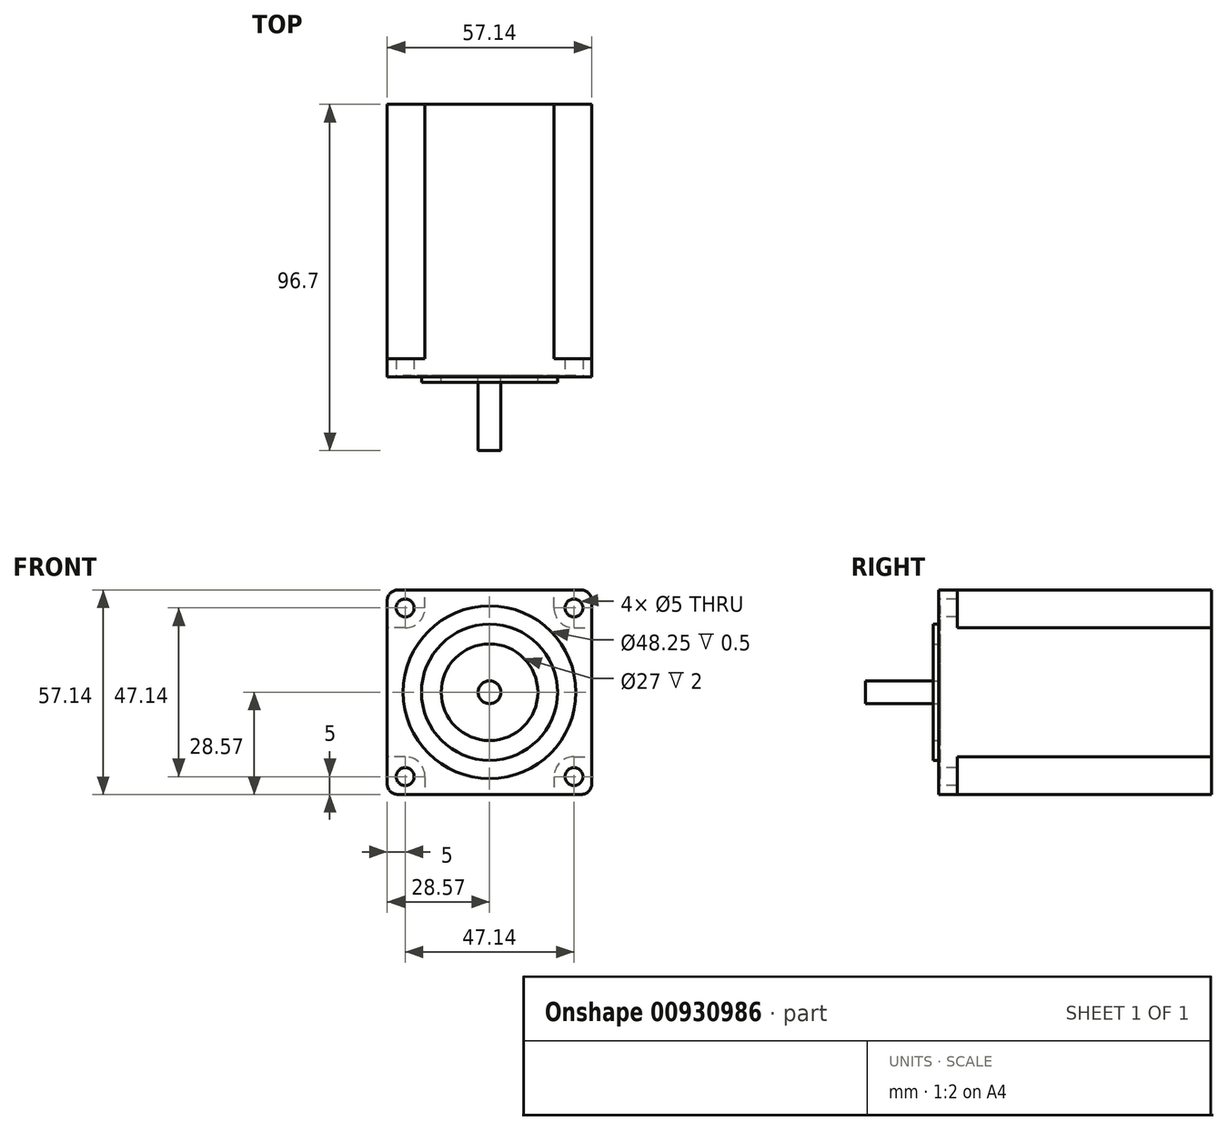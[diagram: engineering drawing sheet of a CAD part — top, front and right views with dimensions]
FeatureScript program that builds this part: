
annotation { "Feature Type Name" : "Feature", "Feature Type Description" : "" }
export const myFeature = defineFeature(function(context is Context, id is Id, definition is map)
    precondition{}
    {
        {
            var Q0;
            Q0=qCreatedBy(makeId("Front.planeOp"),FACE);
            var sketch = newSketch(context, id + "F0", { "sketchPlane" : qUnion([Q0])});
            skLineSegment(sketch, "E0.bottom", {"start": v(28.57, 28.58) * mm, "end": v(-28.58, 28.58) * mm});
            skLineSegment(sketch, "E0.top", {"start": v(28.58, -28.58) * mm, "end": v(-28.57, -28.58) * mm});
            skLineSegment(sketch, "E0.left", {"start": v(28.57, 28.58) * mm, "end": v(28.58, -28.58) * mm});
            skLineSegment(sketch, "E0.right", {"start": v(-28.58, 28.58) * mm, "end": v(-28.57, -28.58) * mm});
            skPoint(sketch, "E0.middle", {"position": v(0, 0) * mm});
            skSolve(sketch);
        }
        {
            var Q0;
            Q0=makeQuery(id+"F0.imprint","IMPRINT",FACE,{"disambiguationData":[TD([[makeQuery(id+"F0.imprint","IMPRINT",EDGE,{"derivedFrom":sQuery(id+"F0.wireOp",EDGE,"E0.bottom")}),1.0]])]});
            extrude(context, id + "F1", {"entities" : qUnion([Q0]), "oppositeDirection" : true, "depth" : 76.2 * mm, "offsetDistance" : 25 * mm});
        }
        {
            var Q0;
            Q0=makeQuery(id+"F1.opExtrude","CAP_FACE",FACE,{"disambiguationData":[OSD([sQuery(id+"F0.wireOp",EDGE,"E0.bottom"),sQuery(id+"F0.wireOp",EDGE,"E0.top"),sQuery(id+"F0.wireOp",EDGE,"E0.left"),sQuery(id+"F0.wireOp",EDGE,"E0.right")])],"isStart":true});
            var sketch = newSketch(context, id + "F2", { "sketchPlane" : qUnion([Q0])});
            skLineSegment(sketch, "E1.bottom", {"start": v(-23.57, 23.57) * mm, "end": v(23.57, 23.57) * mm, "construction": true});
            skLineSegment(sketch, "E1.top", {"start": v(-23.57, -23.57) * mm, "end": v(23.57, -23.57) * mm, "construction": true});
            skLineSegment(sketch, "E1.left", {"start": v(-23.57, 23.57) * mm, "end": v(-23.57, -23.57) * mm, "construction": true});
            skLineSegment(sketch, "E1.right", {"start": v(23.57, 23.57) * mm, "end": v(23.57, -23.57) * mm, "construction": true});
            skPoint(sketch, "E1.middle", {"position": v(0, 0) * mm});
            skCircle(sketch, "E2", {"center": v(-23.57, 23.57) * mm, "radius": 2.5 * mm});
            skCircle(sketch, "E3", {"center": v(23.57, 23.57) * mm, "radius": 2.5 * mm});
            skCircle(sketch, "E4", {"center": v(-23.57, -23.57) * mm, "radius": 2.5 * mm});
            skCircle(sketch, "E5", {"center": v(23.57, -23.57) * mm, "radius": 2.5 * mm});
            skSolve(sketch);
        }
        {
            var Q0;
            Q0 = qSketchRegion(id + "F2", true);
            extrude(context, id + "F3", {"entities" : qUnion([Q0]), "operationType" : NewBodyOperationType.REMOVE, "endBound" : BoundingType.THROUGH_ALL, "oppositeDirection" : true, "depth" : 25 * mm, "offsetDistance" : 25 * mm});
        }
        {
            var Q0;
            Q0=makeQuery(id+"F1.opExtrude","CAP_FACE",FACE,{"disambiguationData":[OSD([sQuery(id+"F0.wireOp",EDGE,"E0.bottom"),sQuery(id+"F0.wireOp",EDGE,"E0.top"),sQuery(id+"F0.wireOp",EDGE,"E0.left"),sQuery(id+"F0.wireOp",EDGE,"E0.right")])],"isStart":false});
            var sketch = newSketch(context, id + "F4", { "sketchPlane" : qUnion([Q0])});
            skArc(sketch, "E6", {"start": v(-23.57, 18.02) * mm, "mid": v(-19.65, 19.65) * mm, "end": v(-18.02, 23.57) * mm});
            skLineSegment(sketch, "E7", {"start": v(-18.02, 23.57) * mm, "end": v(-18.02, 28.58) * mm});
            skLineSegment(sketch, "E8", {"start": v(-23.57, 18.02) * mm, "end": v(-28.57, 18.02) * mm});
            skLineSegment(sketch, "E9", {"start": v(0, 28.58) * mm, "end": v(0, -28.58) * mm, "construction": true});
            skLineSegment(sketch, "E10", {"start": v(0, -28.57) * mm, "end": v(28.57, 0) * mm, "construction": true});
            skLineSegment(sketch, "E11", {"start": v(28.57, 0) * mm, "end": v(-28.57, 0) * mm, "construction": true});
            skLineSegment(sketch, "E12.MirrorCS", {"start": v(18.02, 23.57) * mm, "end": v(18.02, 28.57) * mm});
            skArc(sketch, "E13.MirrorCS", {"start": v(23.57, 18.02) * mm, "mid": v(19.65, 19.65) * mm, "end": v(18.02, 23.57) * mm});
            skLineSegment(sketch, "E14.MirrorCS", {"start": v(23.57, 18.02) * mm, "end": v(28.58, 18.02) * mm});
            skLineSegment(sketch, "E15.MirrorCS", {"start": v(18.02, -23.57) * mm, "end": v(18.02, -28.57) * mm});
            skArc(sketch, "E16.MirrorCS", {"start": v(23.57, -18.02) * mm, "mid": v(19.65, -19.65) * mm, "end": v(18.02, -23.57) * mm});
            skArc(sketch, "E17.MirrorCS", {"start": v(-23.57, -18.02) * mm, "mid": v(-19.65, -19.65) * mm, "end": v(-18.02, -23.57) * mm});
            skLineSegment(sketch, "E18.MirrorCS", {"start": v(23.57, -18.02) * mm, "end": v(28.58, -18.02) * mm});
            skLineSegment(sketch, "E19.MirrorCS", {"start": v(-18.02, -23.57) * mm, "end": v(-18.02, -28.58) * mm});
            skLineSegment(sketch, "E20.MirrorCS", {"start": v(-23.57, -18.02) * mm, "end": v(-28.57, -18.02) * mm});
            skLineSegment(sketch, "E21", {"start": v(-28.57, 18.02) * mm, "end": v(-28.57, 28.58) * mm});
            skLineSegment(sketch, "E22", {"start": v(-28.57, 28.58) * mm, "end": v(-18.02, 28.58) * mm});
            skLineSegment(sketch, "E23", {"start": v(18.02, 28.57) * mm, "end": v(28.58, 28.58) * mm});
            skLineSegment(sketch, "E24", {"start": v(28.58, 28.58) * mm, "end": v(28.58, 18.02) * mm});
            skLineSegment(sketch, "E25", {"start": v(18.02, -28.58) * mm, "end": v(28.57, -28.58) * mm});
            skLineSegment(sketch, "E26", {"start": v(28.57, -28.58) * mm, "end": v(28.58, -18.02) * mm});
            skLineSegment(sketch, "E27", {"start": v(-18.02, -28.58) * mm, "end": v(-28.58, -28.58) * mm});
            skLineSegment(sketch, "E28", {"start": v(-28.58, -28.58) * mm, "end": v(-28.57, -18.02) * mm});
            skSolve(sketch);
        }
        {
            var Q0;
            Q0 = qSketchRegion(id + "F4", true);
            extrude(context, id + "F5", {"entities" : qUnion([Q0]), "operationType" : NewBodyOperationType.REMOVE, "oppositeDirection" : true, "depth" : 71 * mm, "offsetDistance" : 25 * mm});
        }
        {
            var Q0;
            Q0=makeQuery(id+"F5.boolean.opBoolean","COPY",EDGE,{"derivedFrom":makeQuery(id+"F5.opExtrude","SWEPT_EDGE",EDGE,{"disambiguationData":[OSD([sQuery(id+"F0.wireOp",EDGE,"E0.bottom"),sQuery(id+"F4.wireOp",EDGE,"E12.MirrorCS"),sQuery(id+"F4.wireOp",EDGE,"E23")])]})});
            var Q1;
            Q1=makeQuery(id+"F5.boolean.opBoolean","COPY",EDGE,{"derivedFrom":makeQuery(id+"F5.opExtrude","SWEPT_EDGE",EDGE,{"disambiguationData":[OSD([sQuery(id+"F0.wireOp",EDGE,"E0.right"),sQuery(id+"F4.wireOp",EDGE,"E14.MirrorCS"),sQuery(id+"F4.wireOp",EDGE,"E24")])]})});
            var Q2;
            Q2=makeQuery(id+"F1.opExtrude","SWEPT_EDGE",EDGE,{"disambiguationData":[OSD([sQuery(id+"F0.wireOp",EDGE,"E0.bottom"),sQuery(id+"F0.wireOp",EDGE,"E0.right")])]});
            var Q3;
            Q3=makeQuery(id+"F1.opExtrude","SWEPT_EDGE",EDGE,{"disambiguationData":[OSD([sQuery(id+"F0.wireOp",EDGE,"E0.bottom"),sQuery(id+"F0.wireOp",EDGE,"E0.left")])]});
            var Q4;
            Q4=makeQuery(id+"F5.boolean.opBoolean","COPY",EDGE,{"derivedFrom":makeQuery(id+"F5.opExtrude","SWEPT_EDGE",EDGE,{"disambiguationData":[OSD([sQuery(id+"F0.wireOp",EDGE,"E0.bottom"),sQuery(id+"F4.wireOp",EDGE,"E7"),sQuery(id+"F4.wireOp",EDGE,"E22")])]})});
            var Q5;
            Q5=makeQuery(id+"F5.boolean.opBoolean","COPY",EDGE,{"derivedFrom":makeQuery(id+"F5.opExtrude","SWEPT_EDGE",EDGE,{"disambiguationData":[OSD([sQuery(id+"F0.wireOp",EDGE,"E0.left"),sQuery(id+"F4.wireOp",EDGE,"E8"),sQuery(id+"F4.wireOp",EDGE,"E21")])]})});
            var Q6;
            Q6=makeQuery(id+"F1.opExtrude","SWEPT_EDGE",EDGE,{"disambiguationData":[OSD([sQuery(id+"F0.wireOp",EDGE,"E0.top"),sQuery(id+"F0.wireOp",EDGE,"E0.right")])]});
            var Q7;
            Q7=makeQuery(id+"F5.boolean.opBoolean","COPY",EDGE,{"derivedFrom":makeQuery(id+"F5.opExtrude","SWEPT_EDGE",EDGE,{"disambiguationData":[OSD([sQuery(id+"F0.wireOp",EDGE,"E0.right"),sQuery(id+"F4.wireOp",EDGE,"E18.MirrorCS"),sQuery(id+"F4.wireOp",EDGE,"E26")])]})});
            var Q8;
            Q8=makeQuery(id+"F5.boolean.opBoolean","COPY",EDGE,{"derivedFrom":makeQuery(id+"F5.opExtrude","SWEPT_EDGE",EDGE,{"disambiguationData":[OSD([sQuery(id+"F0.wireOp",EDGE,"E0.top"),sQuery(id+"F4.wireOp",EDGE,"E15.MirrorCS"),sQuery(id+"F4.wireOp",EDGE,"E25")])]})});
            var Q9;
            Q9=makeQuery(id+"F1.opExtrude","SWEPT_EDGE",EDGE,{"disambiguationData":[OSD([sQuery(id+"F0.wireOp",EDGE,"E0.top"),sQuery(id+"F0.wireOp",EDGE,"E0.left")])]});
            var Q10;
            Q10=makeQuery(id+"F5.boolean.opBoolean","COPY",EDGE,{"derivedFrom":makeQuery(id+"F5.opExtrude","SWEPT_EDGE",EDGE,{"disambiguationData":[OSD([sQuery(id+"F0.wireOp",EDGE,"E0.left"),sQuery(id+"F4.wireOp",EDGE,"E20.MirrorCS"),sQuery(id+"F4.wireOp",EDGE,"E28")])]})});
            var Q11;
            Q11=makeQuery(id+"F5.boolean.opBoolean","COPY",EDGE,{"derivedFrom":makeQuery(id+"F5.opExtrude","SWEPT_EDGE",EDGE,{"disambiguationData":[OSD([sQuery(id+"F0.wireOp",EDGE,"E0.top"),sQuery(id+"F4.wireOp",EDGE,"E19.MirrorCS"),sQuery(id+"F4.wireOp",EDGE,"E27")])]})});
            fillet(context, id + "F6", {"entities" : qUnion([Q0, Q1, Q2, Q3, Q4, Q5, Q6, Q7, Q8, Q9, Q10, Q11]), "radius" : 3 * mm, "tangentPropagation" : true, "allowEdgeOverflow" : false});
        }
        {
            var Q0;
            Q0=makeQuery(id+"F1.opExtrude","CAP_FACE",FACE,{"disambiguationData":[OSD([sQuery(id+"F0.wireOp",EDGE,"E0.bottom"),sQuery(id+"F0.wireOp",EDGE,"E0.top"),sQuery(id+"F0.wireOp",EDGE,"E0.left"),sQuery(id+"F0.wireOp",EDGE,"E0.right")])],"isStart":true});
            var sketch = newSketch(context, id + "F7", { "sketchPlane" : qUnion([Q0])});
            skCircle(sketch, "E29", {"center": v(0, 0) * mm, "radius": 24.12 * mm});
            skSolve(sketch);
        }
        {
            var Q0;
            Q0 = qSketchRegion(id + "F7", true);
            extrude(context, id + "F8", {"entities" : qUnion([Q0]), "operationType" : NewBodyOperationType.REMOVE, "oppositeDirection" : true, "depth" : 0.5 * mm, "offsetDistance" : 25 * mm});
        }
        {
            var Q0;
            Q0=makeQuery(id+"F8.boolean.opBoolean","COPY",FACE,{"derivedFrom":makeQuery(id+"F8.opExtrude","CAP_FACE",FACE,{"disambiguationData":[OSD([sQuery(id+"F7.wireOp",EDGE,"E29")])],"isStart":false})});
            var sketch = newSketch(context, id + "F9", { "sketchPlane" : qUnion([Q0])});
            skCircle(sketch, "E30", {"center": v(0, 0) * mm, "radius": 19 * mm});
            skCircle(sketch, "E31", {"center": v(0, 0) * mm, "radius": 13.5 * mm});
            skSolve(sketch);
        }
        {
            var Q0;
            Q0 = qSketchRegion(id + "F9", true);
            extrude(context, id + "F10", {"entities" : qUnion([Q0]), "operationType" : NewBodyOperationType.ADD, "depth" : 2 * mm, "offsetDistance" : 25 * mm});
        }
        {
            var Q0;
            Q0=makeQuery(id+"F10.boolean.opBoolean","SPLIT",FACE,{"disambiguationData":[TD([makeQuery(id+"F10.opExtrude","SWEPT_FACE",FACE,{"disambiguationData":[OSD([sQuery(id+"F9.wireOp",EDGE,"E31")])]})])],"derivedFrom":makeQuery(id+"F8.boolean.opBoolean","COPY",FACE,{"derivedFrom":makeQuery(id+"F8.opExtrude","CAP_FACE",FACE,{"disambiguationData":[OSD([sQuery(id+"F7.wireOp",EDGE,"E29")])],"isStart":false})})});
            var sketch = newSketch(context, id + "F11", { "sketchPlane" : qUnion([Q0])});
            skCircle(sketch, "E32", {"center": v(0, 0) * mm, "radius": 3.17 * mm});
            skSolve(sketch);
        }
        {
            var Q0;
            Q0 = qSketchRegion(id + "F11", true);
            extrude(context, id + "F12", {"entities" : qUnion([Q0]), "operationType" : NewBodyOperationType.ADD, "depth" : 21 * mm, "offsetDistance" : 25 * mm});
        }
    });
